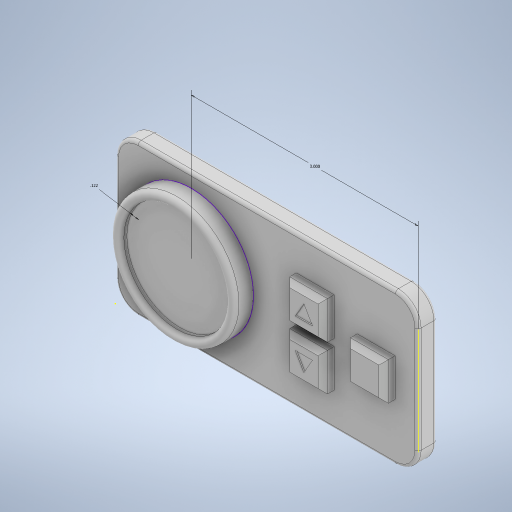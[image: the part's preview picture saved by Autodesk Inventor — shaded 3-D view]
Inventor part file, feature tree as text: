
AUTODESK INVENTOR PART (.ipt)
format: ipt  version: 2023.2 (Build 272271030, 271C)  size: 383,488 bytes
history: native  units: in
note: dims shown in document units (in); Inventor stores cm internally (conversion verified against a paired STEP export)
features: extrude x7, sketch x5, fillet x4, chamfer x3
ambient origin geometry x8: Origin, YZ Plane, XZ Plane, XY Plane, X Axis, Y Axis, Z Axis, Center Point
bodies: Solid1 (feature_tree)
feature tree (19):
  extrude  "Extrusion1"  Depth=2.0in
  fillet  "Fillet1"  Radius=0.25in
  sketch  "Sketch2"  dims[d4=0.3in d5=3.0in]
  extrude  "Extrusion2"  Depth=0.3in
  extrude  "Extrusion3"  Depth=0.25in TaperAngle=0.0deg
  extrude  "Extrusion4"  Depth=0.0609in
  fillet  "Fillet3"  Radius=0.0609in
  extrude  "Extrusion5"  Depth=0.5in
  chamfer  "Chamfer1"  Distance=0.5in
  chamfer  "Chamfer2"  Distance=0.5in
  extrude  "Extrusion6"  Depth=0.454in
  extrude  "Extrusion7"  Depth=0.454in
  chamfer  "Chamfer3"  Distance=0.15in
  fillet  "Fillet4"  Radius=0.0625in
  fillet  "Fillet5"  Radius=0.0625in
  sketch  "Sketch1"  dims[d0=4.0in d1=2.0in d2=0.25in d3=0.0in]
  sketch  "Sketch3"  dims[d6=0.25in d7=0.0in d8=0.25in d9=0.0in]
  sketch  "Sketch4"  dims[d10=0.15in d11=0.0in d13=0.1218in d14=0.0609in]
  sketch  "Sketch5"  dims[d15=0.5in d16=0.5in d17=0.5in d18=0.5in d19=0.454in d20=0.454in d21=0.15in d22=0.0in d23=0.0625in d24=0.125in d25=45.0deg d26=0.0625in d27=0.125in d28=45.0deg d29=60.0deg d30=60.0deg d31=0.074in d33=0.227in d35=0.089in d36=0.1966in d37=0.227in d38=0.227in d39=60.0deg d40=0.089in d41=0.074in d42=0.015in d43=0.0in d44=0.5in d45=0.5in d46=0.75in d47=0.3045in d48=0.15in d49=0.0in d50=0.0625in d51=0.125in d52=45.0deg d53=0.0406in d54=0.0406in]
